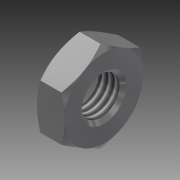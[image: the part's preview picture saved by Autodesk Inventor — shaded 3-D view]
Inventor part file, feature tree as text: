
AUTODESK INVENTOR PART (.ipt)
format: ipt  version: 2016 SP1 (Build 200210100, 210)  size: 138,240 bytes
history: native  units: in
note: dims shown in document units (in); Inventor stores cm internally (conversion verified against a paired STEP export)
features: other x8, revolve x2, sketch x2, extrude x1, thread x1
ambient origin geometry x8: Origin, YZ Plane, XZ Plane, XY Plane, X Axis, Y Axis, Z Axis, Center Point
bodies: Solid1 (feature_tree)
feature tree (14):
  extrude  "Extrusion1"  TaperAngle=360.0deg  [1 undecoded]
  revolve  "Revolution1"  Angle=360.0deg
  thread  "Thread1"  [1 undecoded]
  revolve  "Revolution2"  [1 undecoded]
  other  "conn_XY"
  other  "conn_YZ"
  other  "conn_ZX"
  other  "conn_X"
  other  "conn_Y"
  other  "conn_Z"
  other  "conn_Center"
  sketch  "Sketch_1"  dims[d0=0.156in d1=0.0in d2=360.0deg]
  other  "Fine_Thread"
  sketch  "Sketch_3"  dims[d3=0.1173in d4=0.0in d5=360.0deg d6=0.0in]
note: 3 required parameter values undecoded (feature->parameter linkage not recoverable at this tier; creation-order binding heuristic only, values carry confidence <= 0.55)
